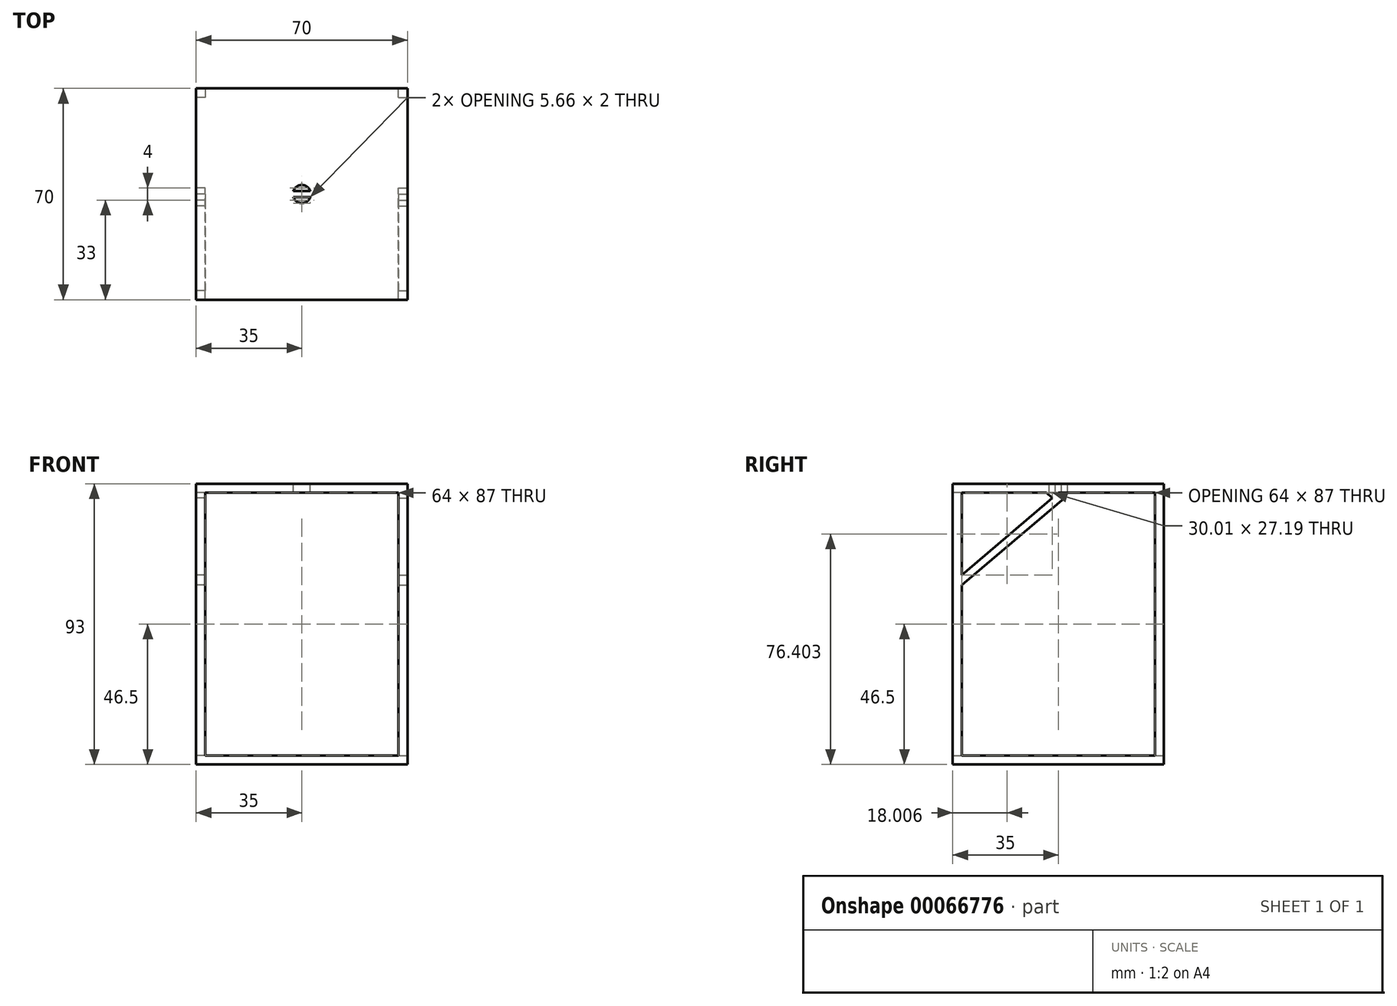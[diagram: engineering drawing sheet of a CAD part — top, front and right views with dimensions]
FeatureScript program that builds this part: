
annotation { "Feature Type Name" : "Feature", "Feature Type Description" : "" }
export const myFeature = defineFeature(function(context is Context, id is Id, definition is map)
    precondition{}
    {
        {
            var Q0;
            Q0=qCreatedBy(makeId("Top.planeOp"),FACE);
            var sketch = newSketch(context, id + "F0", { "sketchPlane" : qUnion([Q0])});
            skLineSegment(sketch, "E0.bottom", {"start": v(-35, 0) * mm, "end": v(0, 0) * mm});
            skLineSegment(sketch, "E0.top", {"start": v(-35, 70) * mm, "end": v(0, 70) * mm});
            skLineSegment(sketch, "E0.left", {"start": v(-35, 0) * mm, "end": v(-35, 70) * mm});
            skLineSegment(sketch, "E0.right", {"start": v(0, 0) * mm, "end": v(0, 70) * mm});
            skSolve(sketch);
        }
        {
            var Q0;
            Q0 = qSketchRegion(id + "F0", true);
            var Q1;
            Q1=makeQuery(id+"F0.imprint","IMPRINT",FACE,{"disambiguationData":[TD([[makeQuery(id+"F0.imprint","IMPRINT",EDGE,{"derivedFrom":sQuery(id+"F0.wireOp",EDGE,"E0.bottom")}),1.0]])]});
            extrude(context, id + "F1", {"entities" : qUnion([Q0, Q1]), "depth" : 3 * mm});
        }
        {
            var Q0;
            Q0=makeQuery(id+"F1.opExtrude","SWEPT_FACE",FACE,{"disambiguationData":[OSD([sQuery(id+"F0.wireOp",EDGE,"E0.left")])]});
            var sketch = newSketch(context, id + "F2", { "sketchPlane" : qUnion([Q0])});
            skLineSegment(sketch, "E1.bottom", {"start": v(-70, 3) * mm, "end": v(0, 3) * mm});
            skLineSegment(sketch, "E1.top", {"start": v(-70, 93) * mm, "end": v(0, 93) * mm});
            skLineSegment(sketch, "E1.left", {"start": v(-70, 3) * mm, "end": v(-70, 93) * mm});
            skLineSegment(sketch, "E1.right", {"start": v(0, 3) * mm, "end": v(0, 93) * mm});
            skLineSegment(sketch, "E2.bottom", {"start": v(-67, 3) * mm, "end": v(-3, 3) * mm});
            skLineSegment(sketch, "E2.top", {"start": v(-67, 90) * mm, "end": v(-3, 90) * mm});
            skLineSegment(sketch, "E2.left", {"start": v(-67, 3) * mm, "end": v(-67, 90) * mm});
            skLineSegment(sketch, "E2.right", {"start": v(-3, 3) * mm, "end": v(-3, 90) * mm});
            skLineSegment(sketch, "E3", {"start": v(-67, 90) * mm, "end": v(-70, 90) * mm});
            skLineSegment(sketch, "E4", {"start": v(-3, 90) * mm, "end": v(0, 90) * mm});
            skLineSegment(sketch, "E5", {"start": v(-35, 90) * mm, "end": v(-35, 93) * mm});
            skPoint(sketch, "E5.startSnap0", {"position": v(-35, 93) * mm});
            skLineSegment(sketch, "E6", {"start": v(-35, 90) * mm, "end": v(-3, 62.8) * mm});
            skLineSegment(sketch, "E7", {"start": v(-3, 62.8) * mm, "end": v(-3, 59.43) * mm});
            skLineSegment(sketch, "E8", {"start": v(-3, 59.43) * mm, "end": v(-38.97, 90) * mm});
            skLineSegment(sketch, "E9", {"start": v(-38.97, 90) * mm, "end": v(-35, 90) * mm});
            skLineSegment(sketch, "E10", {"start": v(-35, 3) * mm, "end": v(-35, 90) * mm, "construction": true});
            skLineSegment(sketch, "E11.MirrorCS", {"start": v(-35, 90) * mm, "end": v(-67, 62.8) * mm});
            skLineSegment(sketch, "E12.MirrorCS", {"start": v(-67, 59.43) * mm, "end": v(-31.03, 90) * mm});
            skLineSegment(sketch, "E13", {"start": v(-38.97, 90) * mm, "end": v(-35, 86.62) * mm});
            skLineSegment(sketch, "E14", {"start": v(-35, 86.62) * mm, "end": v(-31.03, 90) * mm});
            skLineSegment(sketch, "E15", {"start": v(-33.01, 88.31) * mm, "end": v(-3, 62.8) * mm});
            skLineSegment(sketch, "E16", {"start": v(-3, 59.43) * mm, "end": v(-35, 86.62) * mm});
            skLineSegment(sketch, "E17", {"start": v(-67, 59.43) * mm, "end": v(-67, 62.8) * mm});
            skLineSegment(sketch, "E18", {"start": v(-36.99, 88.31) * mm, "end": v(-38.97, 90) * mm});
            skSolve(sketch);
        }
        {
            var Q0;
            Q0=makeQuery(id+"F2.imprint","IMPRINT",FACE,{"disambiguationData":[TD([[makeQuery(id+"F2.imprint","IMPRINT",EDGE,{"derivedFrom":sQuery(id+"F2.wireOp",EDGE,"E7")}),-1.0]])]});
            var Q1;
            Q1=makeQuery(id+"F2.imprint","IMPRINT",FACE,{"disambiguationData":[TD([[makeQuery(id+"F2.imprint","IMPRINT",EDGE,{"derivedFrom":sQuery(id+"F2.wireOp",EDGE,"E12.MirrorCS")}),1.0]])]});
            var Q2;
            {var subQ3=sQuery(id+"F2.wireOp",EDGE,"E3");Q2=makeQuery(id+"F2.imprint","IMPRINT",FACE,{"disambiguationData":[TD([[makeQuery(id+"F2.imprint","IMPRINT",EDGE,{"derivedFrom":subQ3}),-1.0]])]});}
            var Q3;
            {var subQ3=sQuery(id+"F2.wireOp",EDGE,"E4");Q3=makeQuery(id+"F2.imprint","IMPRINT",FACE,{"disambiguationData":[TD([[makeQuery(id+"F2.imprint","IMPRINT",EDGE,{"derivedFrom":subQ3}),1.0]])]});}
            var Q4;
            {var subQ0=sQuery(id+"F2.wireOp",EDGE,"E6");Q4=makeQuery(id+"F2.imprint","IMPRINT",FACE,{"disambiguationData":[TD([[makeQuery(id+"F2.imprint","IMPRINT",EDGE,{"derivedFrom":subQ0}),1.0]])]});}
            var Q5;
            {var subQ0=sQuery(id+"F2.wireOp",EDGE,"E6");Q5=makeQuery(id+"F2.imprint","IMPRINT",FACE,{"disambiguationData":[TD([[makeQuery(id+"F2.imprint","IMPRINT",EDGE,{"derivedFrom":subQ0}),-1.0]])]});}
            var Q6;
            {var subQ0=sQuery(id+"F2.wireOp",EDGE,"E9");Q6=makeQuery(id+"F2.imprint","IMPRINT",FACE,{"disambiguationData":[TD([[makeQuery(id+"F2.imprint","IMPRINT",EDGE,{"derivedFrom":subQ0}),-1.0]])]});}
            var Q7;
            {var subQ0=sQuery(id+"F2.wireOp",EDGE,"E3");Q7=makeQuery(id+"F2.imprint","IMPRINT",FACE,{"disambiguationData":[TD([[makeQuery(id+"F2.imprint","IMPRINT",EDGE,{"derivedFrom":subQ0}),1.0]])]});}
            var Q8;
            {var subQ0=sQuery(id+"F2.wireOp",EDGE,"E4");Q8=makeQuery(id+"F2.imprint","IMPRINT",FACE,{"disambiguationData":[TD([[makeQuery(id+"F2.imprint","IMPRINT",EDGE,{"derivedFrom":subQ0}),-1.0]])]});}
            extrude(context, id + "F3", {"entities" : qUnion([Q0, Q1, Q2, Q3, Q4, Q5, Q6, Q7, Q8]), "operationType" : NewBodyOperationType.ADD, "oppositeDirection" : true, "depth" : 3 * mm});
        }
        {
            var Q0;
            Q0=makeQuery(id+"F3.opExtrude","SWEPT_FACE",FACE,{"disambiguationData":[OSD([sQuery(id+"F2.wireOp",EDGE,"E1.top")])]});
            var sketch = newSketch(context, id + "F4", { "sketchPlane" : qUnion([Q0])});
            skLineSegment(sketch, "E19.bottom", {"start": v(-35, 0) * mm, "end": v(0, 0) * mm});
            skLineSegment(sketch, "E19.top", {"start": v(-35, 70) * mm, "end": v(0, 70) * mm});
            skLineSegment(sketch, "E19.left", {"start": v(-35, 0) * mm, "end": v(-35, 70) * mm});
            skLineSegment(sketch, "E19.right", {"start": v(0, 0) * mm, "end": v(0, 70) * mm});
            skCircle(sketch, "E20", {"center": v(0, 35) * mm, "radius": 3 * mm});
            skLineSegment(sketch, "E21.rect.bottom", {"start": v(2.83, 34) * mm, "end": v(-2.83, 34) * mm});
            skLineSegment(sketch, "E21.rect.top", {"start": v(2.83, 36) * mm, "end": v(-2.83, 36) * mm});
            skSolve(sketch);
        }
        {
            var Q0;
            {var subQ2=sQuery(id+"F4.wireOp",EDGE,"E19.right");Q0=makeQuery(id+"F4.imprint","IMPRINT",FACE,{"disambiguationData":[TD([[makeQuery(id+"F4.imprint","IMPRINT",EDGE,{"derivedFrom":subQ2}),1.0]])]});}
            var Q1;
            {var subQ5=sQuery(id+"F4.wireOp",EDGE,"E21.rect.right");Q1=makeQuery(id+"F4.imprint","IMPRINT",FACE,{"disambiguationData":[TD([[makeQuery(id+"F4.imprint","IMPRINT",EDGE,{"derivedFrom":subQ5}),-1.0]])]});}
            var Q2;
            {var subQ0=sQuery(id+"F4.wireOp",EDGE,"E21.rect.bottom");var subQ1=sQuery(id+"F4.wireOp",EDGE,"E19.right");var subQ2=makeQuery(id+"F4.imprint","INTERSECT",VERTEX,{"derivedFrom":[subQ1,subQ0]});Q2=makeQuery(id+"F4.imprint","IMPRINT",FACE,{"disambiguationData":[TD([[makeQuery(id+"F4.imprint","IMPRINT",EDGE,{"disambiguationData":[TD([[subQ2,-1.0]])],"derivedFrom":subQ1}),1.0]])]});}
            extrude(context, id + "F5", {"entities" : qUnion([Q0, Q1, Q2]), "operationType" : NewBodyOperationType.ADD, "oppositeDirection" : true, "depth" : 3 * mm});
        }
        {
            var Q0;
            Q0=makeQuery(id+"F3.opExtrude","SWEPT_BODY",BODY,{"disambiguationData":[OSD([sQuery(id+"F2.wireOp",EDGE,"E1.bottom"),sQuery(id+"F2.wireOp",EDGE,"E1.top"),sQuery(id+"F2.wireOp",EDGE,"E1.left"),sQuery(id+"F2.wireOp",EDGE,"E1.right"),sQuery(id+"F2.wireOp",EDGE,"E2.top"),sQuery(id+"F2.wireOp",EDGE,"E2.left"),sQuery(id+"F2.wireOp",EDGE,"E2.right"),sQuery(id+"F2.wireOp",EDGE,"E11.MirrorCS"),sQuery(id+"F2.wireOp",EDGE,"E12.MirrorCS"),sQuery(id+"F2.wireOp",EDGE,"E14"),sQuery(id+"F2.wireOp",EDGE,"E15"),sQuery(id+"F2.wireOp",EDGE,"E16"),sQuery(id+"F2.wireOp",EDGE,"E18")])]});
            var Q1;
            Q1=makeQuery(id+"F1.opExtrude","SWEPT_BODY",BODY,{"disambiguationData":[OSD([sQuery(id+"F0.wireOp",EDGE,"E0.bottom"),sQuery(id+"F0.wireOp",EDGE,"E0.top"),sQuery(id+"F0.wireOp",EDGE,"E0.left"),sQuery(id+"F0.wireOp",EDGE,"E0.right")])]});
            var Q2;
            Q2=makeQuery(id+"F5.opExtrude","SWEPT_BODY",BODY,{"disambiguationData":[OSD([sQuery(id+"F2.wireOp",EDGE,"E1.top"),sQuery(id+"F4.wireOp",EDGE,"E19.bottom"),sQuery(id+"F4.wireOp",EDGE,"E19.top"),sQuery(id+"F4.wireOp",EDGE,"E19.right")])]});
            var Q3;
            Q3=qCreatedBy(makeId("Right.planeOp"),FACE);
            mirror(context, id + "F6", {"operationType" : NewBodyOperationType.ADD, "entities" : qUnion([Q0, Q1, Q2]), "mirrorPlane" : qUnion([Q3])});
        }
    });
